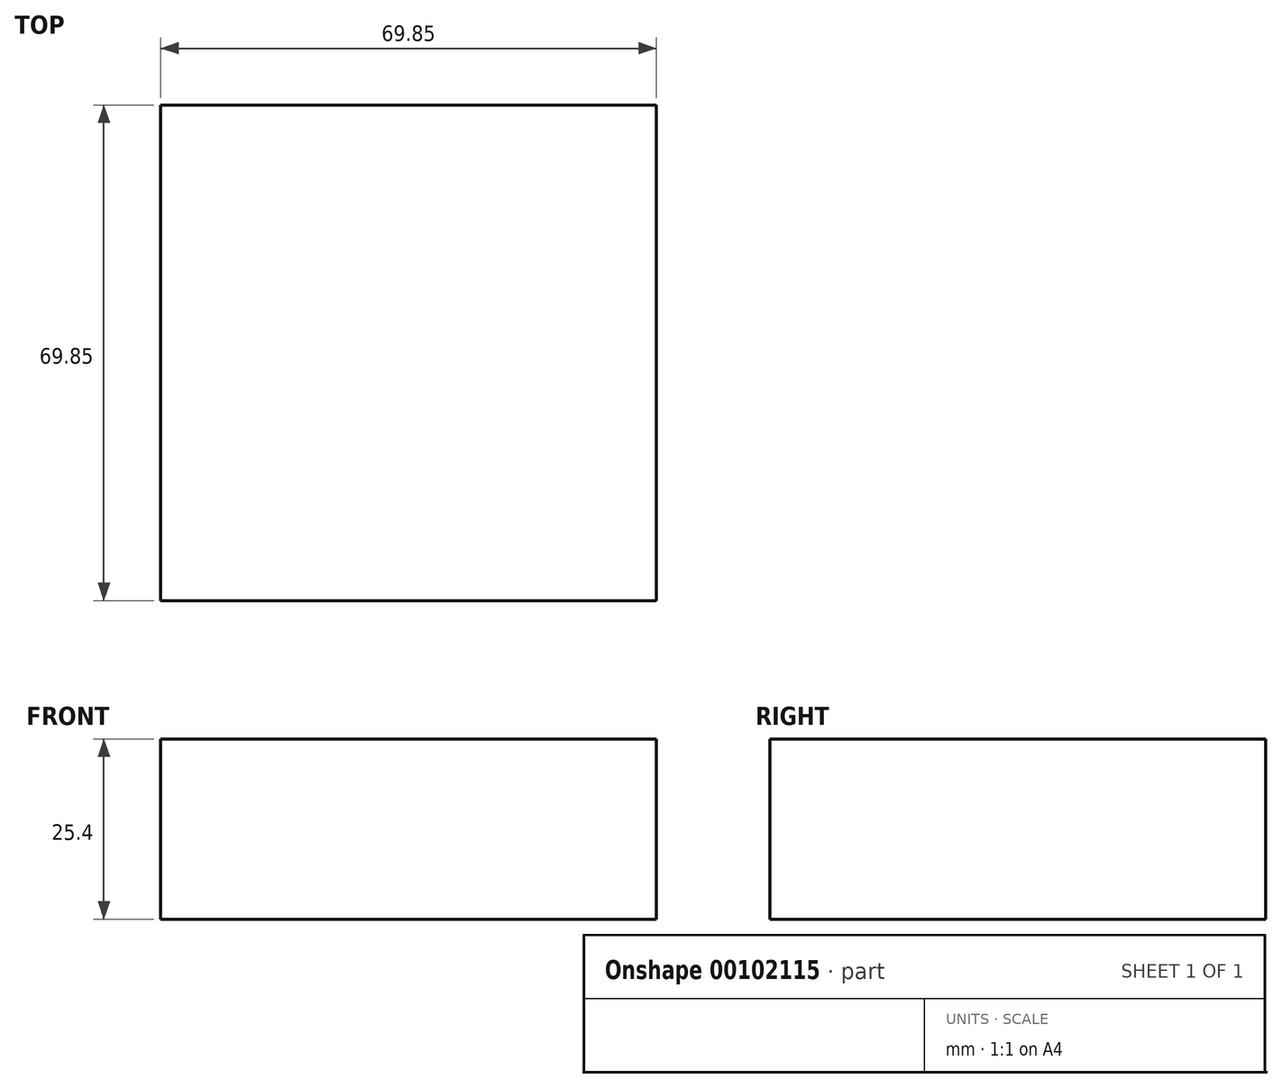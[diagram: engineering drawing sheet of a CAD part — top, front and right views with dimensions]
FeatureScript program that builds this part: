
annotation { "Feature Type Name" : "Feature", "Feature Type Description" : "" }
export const myFeature = defineFeature(function(context is Context, id is Id, definition is map)
    precondition{}
    {
        {
            var Q0;
            Q0=qCreatedBy(makeId("Top.planeOp"),FACE);
            var sketch = newSketch(context, id + "F0", { "sketchPlane" : qUnion([Q0])});
            skLineSegment(sketch, "E0.bottom", {"start": v(-31.46, 46.87) * mm, "end": v(38.39, 46.87) * mm});
            skLineSegment(sketch, "E0.top", {"start": v(-31.46, -22.98) * mm, "end": v(38.39, -22.98) * mm});
            skLineSegment(sketch, "E0.left", {"start": v(-31.46, 46.87) * mm, "end": v(-31.46, -22.98) * mm});
            skLineSegment(sketch, "E0.right", {"start": v(38.39, 46.87) * mm, "end": v(38.39, -22.98) * mm});
            skSolve(sketch);
        }
        {
            var Q0;
            Q0=makeQuery(id+"F0.imprint","IMPRINT",FACE,{"disambiguationData":[TD([[makeQuery(id+"F0.imprint","IMPRINT",EDGE,{"derivedFrom":sQuery(id+"F0.wireOp",EDGE,"E0.bottom")}),-1.0]])]});
            extrude(context, id + "F1", {"entities" : qUnion([Q0]), "depth" : 25.4 * mm});
        }
    });
